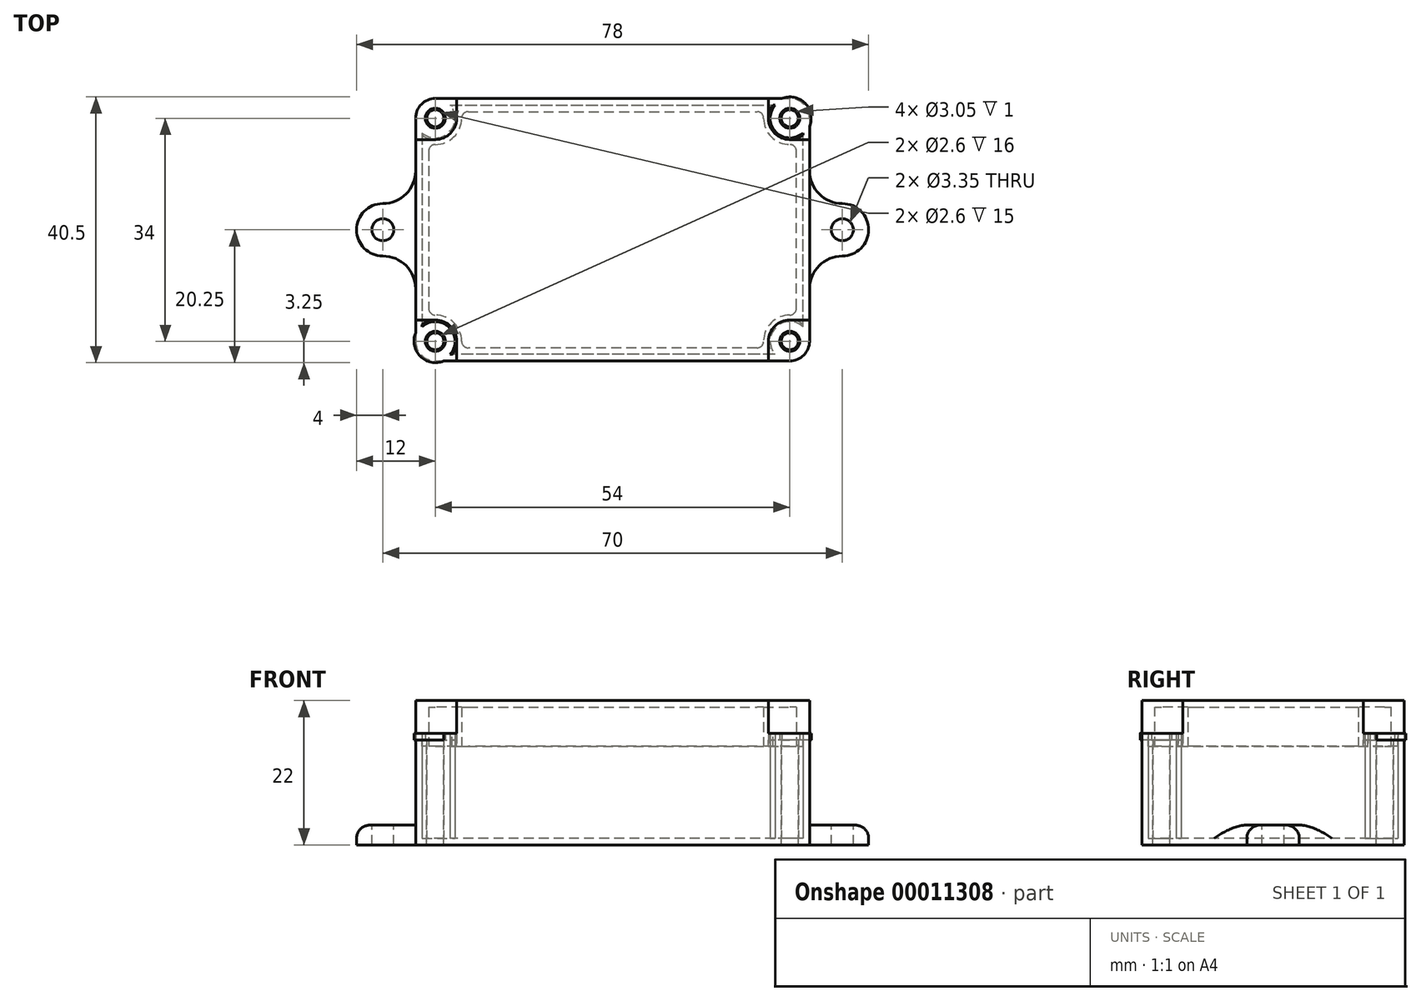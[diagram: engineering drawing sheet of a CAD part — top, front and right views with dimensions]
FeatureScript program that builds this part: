
annotation { "Feature Type Name" : "Feature", "Feature Type Description" : "" }
export const myFeature = defineFeature(function(context is Context, id is Id, definition is map)
    precondition{}
    {
        {
            var Q0;
            Q0=qCreatedBy(makeId("Top.planeOp"),FACE);
            var sketch = newSketch(context, id + "F0", { "sketchPlane" : qUnion([Q0])});
            skLineSegment(sketch, "E0.bottom", {"start": v(-27, 20) * mm, "end": v(27, 20) * mm});
            skLineSegment(sketch, "E0.top", {"start": v(-27, -20) * mm, "end": v(27, -20) * mm});
            skLineSegment(sketch, "E0.left", {"start": v(-30, 17) * mm, "end": v(-30, -17) * mm});
            skLineSegment(sketch, "E0.right", {"start": v(30, 17) * mm, "end": v(30, -17) * mm});
            skLineSegment(sketch, "E1", {"start": v(0, 0) * mm, "end": v(0, 30.82) * mm, "construction": true});
            skLineSegment(sketch, "E2", {"start": v(0, 0) * mm, "end": v(-60.1, 0) * mm, "construction": true});
            skArc(sketch, "E3", {"start": v(-27, 20) * mm, "mid": v(-29.12, 19.12) * mm, "end": v(-30, 17) * mm});
            skLineSegment(sketch, "E4", {"start": v(-30, -4) * mm, "end": v(-35, -4) * mm});
            skLineSegment(sketch, "E5", {"start": v(-30, 4) * mm, "end": v(-35, 4) * mm});
            skArc(sketch, "E6", {"start": v(-35, 4) * mm, "mid": v(-39, 0) * mm, "end": v(-35, -4) * mm});
            skCircle(sketch, "E7", {"center": v(-35, 0) * mm, "radius": 1.68 * mm});
            skLineSegment(sketch, "E8.0.MirrorCS", {"start": v(30, 4) * mm, "end": v(35, 4) * mm});
            skArc(sketch, "E9.0.MirrorCS", {"start": v(35, 4) * mm, "mid": v(39, 0) * mm, "end": v(35, -4) * mm});
            skCircle(sketch, "E10.0.MirrorC", {"center": v(35, 0) * mm, "radius": 1.68 * mm});
            skLineSegment(sketch, "E11.0.MirrorCS", {"start": v(30, -4) * mm, "end": v(35, -4) * mm});
            skCircle(sketch, "E12", {"center": v(-27, 17) * mm, "radius": 1.3 * mm});
            skLineSegment(sketch, "E13", {"start": v(-24.76, 19) * mm, "end": v(0, 19) * mm});
            skLineSegment(sketch, "E14", {"start": v(-29, 0) * mm, "end": v(-29, 14.76) * mm});
            skArc(sketch, "E15.trimOffspring", {"start": v(-29, 14.76) * mm, "mid": v(-24.88, 14.88) * mm, "end": v(-24.76, 19) * mm});
            skLineSegment(sketch, "E16.0.MirrorCS", {"start": v(24.76, 19) * mm, "end": v(0, 19) * mm});
            skArc(sketch, "E17.0.MirrorCS", {"start": v(29, 14.76) * mm, "mid": v(24.88, 14.88) * mm, "end": v(24.76, 19) * mm});
            skLineSegment(sketch, "E18.0.MirrorCS", {"start": v(29, 0) * mm, "end": v(29, 14.76) * mm});
            skCircle(sketch, "E19.0.MirrorC", {"center": v(27, 17) * mm, "radius": 1.3 * mm});
            skArc(sketch, "E20.0.MirrorCS", {"start": v(27, 20) * mm, "mid": v(29.12, 19.12) * mm, "end": v(30, 17) * mm});
            skLineSegment(sketch, "E21.0.MirrorCS", {"start": v(-29, 0) * mm, "end": v(-29, -14.76) * mm});
            skArc(sketch, "E22.0.MirrorCS", {"start": v(-29, -14.76) * mm, "mid": v(-24.88, -14.88) * mm, "end": v(-24.76, -19) * mm});
            skCircle(sketch, "E23.0.MirrorC", {"center": v(-27, -17) * mm, "radius": 1.3 * mm});
            skArc(sketch, "E24.0.MirrorCS", {"start": v(-27, -20) * mm, "mid": v(-29.12, -19.12) * mm, "end": v(-30, -17) * mm});
            skLineSegment(sketch, "E25.0.MirrorCS", {"start": v(-24.76, -19) * mm, "end": v(0, -19) * mm});
            skArc(sketch, "E26.0.MirrorCS", {"start": v(29, -14.76) * mm, "mid": v(24.88, -14.88) * mm, "end": v(24.76, -19) * mm});
            skCircle(sketch, "E27.0.MirrorC", {"center": v(27, -17) * mm, "radius": 1.3 * mm});
            skLineSegment(sketch, "E28.0.MirrorCS", {"start": v(24.76, -19) * mm, "end": v(0, -19) * mm});
            skLineSegment(sketch, "E29.0.MirrorCS", {"start": v(29, 0) * mm, "end": v(29, -14.76) * mm});
            skArc(sketch, "E30.0.MirrorCS", {"start": v(27, -20) * mm, "mid": v(29.12, -19.12) * mm, "end": v(30, -17) * mm});
            skSolve(sketch);
        }
        {
            var Q0;
            {var subQ1=sQuery(id+"F0.wireOp",EDGE,"E4");Q0=makeQuery(id+"F0.imprint","IMPRINT",FACE,{"disambiguationData":[TD([[makeQuery(id+"F0.imprint","IMPRINT",EDGE,{"derivedFrom":subQ1}),-1.0]])]});}
            var Q1;
            Q1=makeQuery(id+"F0.imprint","IMPRINT",FACE,{"disambiguationData":[TD([[makeQuery(id+"F0.imprint","IMPRINT",EDGE,{"derivedFrom":sQuery(id+"F0.wireOp",EDGE,"E0.bottom")}),-1.0]])]});
            var Q2;
            Q2=makeQuery(id+"F0.imprint","IMPRINT",FACE,{"disambiguationData":[TD([[makeQuery(id+"F0.imprint","IMPRINT",EDGE,{"derivedFrom":sQuery(id+"F0.wireOp",EDGE,"E12")}),1.0]])]});
            var Q3;
            Q3=makeQuery(id+"F0.imprint","IMPRINT",FACE,{"disambiguationData":[TD([[makeQuery(id+"F0.imprint","IMPRINT",EDGE,{"derivedFrom":sQuery(id+"F0.wireOp",EDGE,"E23.0.MirrorC")}),-1.0]])]});
            var Q4;
            Q4=makeQuery(id+"F0.imprint","IMPRINT",FACE,{"disambiguationData":[TD([[makeQuery(id+"F0.imprint","IMPRINT",EDGE,{"derivedFrom":sQuery(id+"F0.wireOp",EDGE,"E13")}),-1.0]])]});
            var Q5;
            Q5=makeQuery(id+"F0.imprint","IMPRINT",FACE,{"disambiguationData":[TD([[makeQuery(id+"F0.imprint","IMPRINT",EDGE,{"derivedFrom":sQuery(id+"F0.wireOp",EDGE,"E19.0.MirrorC")}),-1.0]])]});
            var Q6;
            Q6=makeQuery(id+"F0.imprint","IMPRINT",FACE,{"disambiguationData":[TD([[makeQuery(id+"F0.imprint","IMPRINT",EDGE,{"derivedFrom":sQuery(id+"F0.wireOp",EDGE,"E27.0.MirrorC")}),1.0]])]});
            var Q7;
            {var subQ1=sQuery(id+"F0.wireOp",EDGE,"E8.0.MirrorCS");Q7=makeQuery(id+"F0.imprint","IMPRINT",FACE,{"disambiguationData":[TD([[makeQuery(id+"F0.imprint","IMPRINT",EDGE,{"derivedFrom":subQ1}),-1.0]])]});}
            extrude(context, id + "F1", {"entities" : qUnion([Q0, Q1, Q2, Q3, Q4, Q5, Q6, Q7]), "oppositeDirection" : true, "depth" : 1 * mm});
        }
        {
            var Q0;
            Q0=makeQuery(id+"F1.opExtrude","SWEPT_EDGE",EDGE,{"disambiguationData":[OSD([sQuery(id+"F0.wireOp",EDGE,"E0.left"),sQuery(id+"F0.wireOp",EDGE,"E5")])]});
            var Q1;
            Q1=makeQuery(id+"F1.opExtrude","SWEPT_EDGE",EDGE,{"disambiguationData":[OSD([sQuery(id+"F0.wireOp",EDGE,"E0.left"),sQuery(id+"F0.wireOp",EDGE,"E4")])]});
            var Q2;
            Q2=makeQuery(id+"F1.opExtrude","SWEPT_EDGE",EDGE,{"disambiguationData":[OSD([sQuery(id+"F0.wireOp",EDGE,"E0.right"),sQuery(id+"F0.wireOp",EDGE,"E11.0.MirrorCS")])]});
            var Q3;
            Q3=makeQuery(id+"F1.opExtrude","SWEPT_EDGE",EDGE,{"disambiguationData":[OSD([sQuery(id+"F0.wireOp",EDGE,"E0.right"),sQuery(id+"F0.wireOp",EDGE,"E8.0.MirrorCS")])]});
            fillet(context, id + "F2", {"entities" : qUnion([Q0, Q1, Q2, Q3]), "radius" : 5 * mm, "tangentPropagation" : true, "allowEdgeOverflow" : false});
        }
        {
            var Q0;
            Q0=makeQuery(id+"F0.imprint","IMPRINT",FACE,{"disambiguationData":[TD([[makeQuery(id+"F0.imprint","IMPRINT",EDGE,{"derivedFrom":sQuery(id+"F0.wireOp",EDGE,"E0.bottom")}),-1.0]])]});
            extrude(context, id + "F3", {"entities" : qUnion([Q0]), "operationType" : NewBodyOperationType.ADD, "depth" : 15 * mm});
        }
        {
            var Q0;
            {var subQ0=sQuery(id+"F0.wireOp",EDGE,"E0.left");var subQ1=sQuery(id+"F0.wireOp",EDGE,"E3");var subQ2=sQuery(id+"F0.wireOp",EDGE,"E4");var subQ3=sQuery(id+"F0.wireOp",EDGE,"E5");var subQ4=sQuery(id+"F0.wireOp",EDGE,"E6");var subQ5=sQuery(id+"F0.wireOp",EDGE,"E7");var subQ6=sQuery(id+"F0.wireOp",EDGE,"E24.0.MirrorCS");Q0=makeQuery(id+"F3.boolean.opBoolean","SPLIT",FACE,{"disambiguationData":[TD([makeQuery(id+"F1.opExtrude","SWEPT_FACE",FACE,{"disambiguationData":[OSD([subQ4])]})])],"derivedFrom":makeQuery(id+"F1.opExtrude","CAP_FACE",FACE,{"disambiguationData":[OSD([sQuery(id+"F0.wireOp",EDGE,"E0.bottom"),sQuery(id+"F0.wireOp",EDGE,"E0.top"),subQ0,sQuery(id+"F0.wireOp",EDGE,"E0.right"),subQ1,subQ2,subQ3,subQ4,subQ5,sQuery(id+"F0.wireOp",EDGE,"E8.0.MirrorCS"),sQuery(id+"F0.wireOp",EDGE,"E9.0.MirrorCS"),sQuery(id+"F0.wireOp",EDGE,"E10.0.MirrorC"),sQuery(id+"F0.wireOp",EDGE,"E11.0.MirrorCS"),sQuery(id+"F0.wireOp",EDGE,"E20.0.MirrorCS"),subQ6,sQuery(id+"F0.wireOp",EDGE,"E30.0.MirrorCS")])],"isStart":true})});}
            var Q1;
            {var subQ0=sQuery(id+"F0.wireOp",EDGE,"E0.right");var subQ1=sQuery(id+"F0.wireOp",EDGE,"E8.0.MirrorCS");var subQ2=sQuery(id+"F0.wireOp",EDGE,"E9.0.MirrorCS");var subQ3=sQuery(id+"F0.wireOp",EDGE,"E10.0.MirrorC");var subQ4=sQuery(id+"F0.wireOp",EDGE,"E11.0.MirrorCS");var subQ5=sQuery(id+"F0.wireOp",EDGE,"E20.0.MirrorCS");var subQ6=sQuery(id+"F0.wireOp",EDGE,"E30.0.MirrorCS");Q1=makeQuery(id+"F3.boolean.opBoolean","SPLIT",FACE,{"disambiguationData":[TD([makeQuery(id+"F1.opExtrude","SWEPT_FACE",FACE,{"disambiguationData":[OSD([subQ2])]})])],"derivedFrom":makeQuery(id+"F1.opExtrude","CAP_FACE",FACE,{"disambiguationData":[OSD([sQuery(id+"F0.wireOp",EDGE,"E0.bottom"),sQuery(id+"F0.wireOp",EDGE,"E0.top"),sQuery(id+"F0.wireOp",EDGE,"E0.left"),subQ0,sQuery(id+"F0.wireOp",EDGE,"E3"),sQuery(id+"F0.wireOp",EDGE,"E4"),sQuery(id+"F0.wireOp",EDGE,"E5"),sQuery(id+"F0.wireOp",EDGE,"E6"),sQuery(id+"F0.wireOp",EDGE,"E7"),subQ1,subQ2,subQ3,subQ4,subQ5,sQuery(id+"F0.wireOp",EDGE,"E24.0.MirrorCS"),subQ6])],"isStart":true})});}
            extrude(context, id + "F4", {"entities" : qUnion([Q0, Q1]), "operationType" : NewBodyOperationType.ADD, "depth" : 2 * mm});
        }
        {
            var Q0;
            Q0=makeQuery(id+"F4.opExtrude","CAP_EDGE",EDGE,{"disambiguationData":[OSD([sQuery(id+"F0.wireOp",EDGE,"E0.left")])],"isStart":false});
            var Q1;
            Q1=makeQuery(id+"F4.opExtrude","CAP_EDGE",EDGE,{"disambiguationData":[OSD([sQuery(id+"F0.wireOp",EDGE,"E0.right")])],"isStart":false});
            fillet(context, id + "F5", {"entities" : qUnion([Q0, Q1]), "radius" : 2 * mm, "tangentPropagation" : true, "allowEdgeOverflow" : false});
        }
        {
            var Q0;
            Q0=makeQuery(id+"F3.opExtrude","CAP_FACE",FACE,{"disambiguationData":[OSD([sQuery(id+"F0.wireOp",EDGE,"E0.bottom"),sQuery(id+"F0.wireOp",EDGE,"E0.top"),sQuery(id+"F0.wireOp",EDGE,"E0.left"),sQuery(id+"F0.wireOp",EDGE,"E0.right"),sQuery(id+"F0.wireOp",EDGE,"E3"),sQuery(id+"F0.wireOp",EDGE,"E12"),sQuery(id+"F0.wireOp",EDGE,"E13"),sQuery(id+"F0.wireOp",EDGE,"E14"),sQuery(id+"F0.wireOp",EDGE,"E15.trimOffspring"),sQuery(id+"F0.wireOp",EDGE,"E16.0.MirrorCS"),sQuery(id+"F0.wireOp",EDGE,"E17.0.MirrorCS"),sQuery(id+"F0.wireOp",EDGE,"E18.0.MirrorCS"),sQuery(id+"F0.wireOp",EDGE,"E19.0.MirrorC"),sQuery(id+"F0.wireOp",EDGE,"E20.0.MirrorCS"),sQuery(id+"F0.wireOp",EDGE,"E21.0.MirrorCS"),sQuery(id+"F0.wireOp",EDGE,"E22.0.MirrorCS"),sQuery(id+"F0.wireOp",EDGE,"E23.0.MirrorC"),sQuery(id+"F0.wireOp",EDGE,"E24.0.MirrorCS"),sQuery(id+"F0.wireOp",EDGE,"E25.0.MirrorCS"),sQuery(id+"F0.wireOp",EDGE,"E26.0.MirrorCS"),sQuery(id+"F0.wireOp",EDGE,"E27.0.MirrorC"),sQuery(id+"F0.wireOp",EDGE,"E28.0.MirrorCS"),sQuery(id+"F0.wireOp",EDGE,"E29.0.MirrorCS"),sQuery(id+"F0.wireOp",EDGE,"E30.0.MirrorCS")])],"isStart":false});
            var sketch = newSketch(context, id + "F6", { "sketchPlane" : qUnion([Q0])});
            skLineSegment(sketch, "E31.1", {"start": v(-27, 20) * mm, "end": v(27, 20) * mm});
            skArc(sketch, "E31.2", {"start": v(-27, 20) * mm, "mid": v(-29.12, 19.12) * mm, "end": v(-30, 17) * mm});
            skLineSegment(sketch, "E31.3", {"start": v(-30, 17) * mm, "end": v(-30, -17) * mm});
            skArc(sketch, "E31.4", {"start": v(-27, -20) * mm, "mid": v(-29.12, -19.12) * mm, "end": v(-30, -17) * mm});
            skLineSegment(sketch, "E31.5", {"start": v(-27, -20) * mm, "end": v(27, -20) * mm});
            skArc(sketch, "E31.6", {"start": v(27, -20) * mm, "mid": v(29.12, -19.12) * mm, "end": v(30, -17) * mm});
            skLineSegment(sketch, "E31.7", {"start": v(30, 17) * mm, "end": v(30, -17) * mm});
            skArc(sketch, "E31.8", {"start": v(27, 20) * mm, "mid": v(29.12, 19.12) * mm, "end": v(30, 17) * mm});
            skCircle(sketch, "E31.9", {"center": v(27, 17) * mm, "radius": 1.3 * mm});
            skArc(sketch, "E31.10", {"start": v(29, 14.76) * mm, "mid": v(24.88, 14.88) * mm, "end": v(24.76, 19) * mm});
            skLineSegment(sketch, "E31.11", {"start": v(29, -14.76) * mm, "end": v(29, 14.76) * mm});
            skArc(sketch, "E31.12", {"start": v(29, -14.76) * mm, "mid": v(24.88, -14.88) * mm, "end": v(24.76, -19) * mm});
            skLineSegment(sketch, "E31.13", {"start": v(24.76, -19) * mm, "end": v(-24.76, -19) * mm});
            skCircle(sketch, "E31.14", {"center": v(27, -17) * mm, "radius": 1.3 * mm});
            skArc(sketch, "E31.15", {"start": v(-29, -14.76) * mm, "mid": v(-24.88, -14.88) * mm, "end": v(-24.76, -19) * mm});
            skCircle(sketch, "E31.16", {"center": v(-27, -17) * mm, "radius": 1.3 * mm});
            skLineSegment(sketch, "E31.17", {"start": v(-29, 14.76) * mm, "end": v(-29, -14.76) * mm});
            skArc(sketch, "E31.18", {"start": v(-29, 14.76) * mm, "mid": v(-24.88, 14.88) * mm, "end": v(-24.76, 19) * mm});
            skCircle(sketch, "E31.20", {"center": v(-27, 17) * mm, "radius": 1.3 * mm});
            skLineSegment(sketch, "E31.21", {"start": v(-24.76, 19) * mm, "end": v(24.76, 19) * mm});
            skLineSegment(sketch, "E32.0", {"start": v(0, 0) * mm, "end": v(0, 30.82) * mm, "construction": true});
            skLineSegment(sketch, "E32.1", {"start": v(0, 0) * mm, "end": v(-60.1, 0) * mm, "construction": true});
            skCircle(sketch, "E33", {"center": v(-27, 17) * mm, "radius": 3.25 * mm});
            skCircle(sketch, "E34", {"center": v(-27, 17) * mm, "radius": 1.52 * mm});
            skCircle(sketch, "E35.0.MirrorC", {"center": v(27, 17) * mm, "radius": 1.52 * mm});
            skCircle(sketch, "E36.0.MirrorC", {"center": v(27, 17) * mm, "radius": 3.25 * mm});
            skCircle(sketch, "E37.0.MirrorC", {"center": v(-27, -17) * mm, "radius": 1.52 * mm});
            skCircle(sketch, "E38.0.MirrorC", {"center": v(-27, -17) * mm, "radius": 3.25 * mm});
            skCircle(sketch, "E39.0.MirrorC", {"center": v(27, -17) * mm, "radius": 1.52 * mm});
            skCircle(sketch, "E40.0.MirrorC", {"center": v(27, -17) * mm, "radius": 3.25 * mm});
            skArc(sketch, "E41.0", {"start": v(-28, 13.13) * mm, "mid": v(-24.17, 14.17) * mm, "end": v(-23.13, 18) * mm});
            skLineSegment(sketch, "E41.1", {"start": v(-28, 13.13) * mm, "end": v(-28, -13.13) * mm});
            skArc(sketch, "E41.2", {"start": v(-28, -13.13) * mm, "mid": v(-24.17, -14.17) * mm, "end": v(-23.13, -18) * mm});
            skLineSegment(sketch, "E41.3", {"start": v(23.13, -18) * mm, "end": v(-23.13, -18) * mm});
            skArc(sketch, "E41.4", {"start": v(28, -13.13) * mm, "mid": v(24.17, -14.17) * mm, "end": v(23.13, -18) * mm});
            skLineSegment(sketch, "E41.5", {"start": v(-23.13, 18) * mm, "end": v(23.13, 18) * mm});
            skLineSegment(sketch, "E41.6", {"start": v(28, -13.13) * mm, "end": v(28, 13.13) * mm});
            skArc(sketch, "E41.7", {"start": v(28, 13.13) * mm, "mid": v(24.17, 14.17) * mm, "end": v(23.13, 18) * mm});
            skLineSegment(sketch, "E42", {"start": v(-30, 13.75) * mm, "end": v(-27, 13.75) * mm});
            skLineSegment(sketch, "E43", {"start": v(-23.75, 20) * mm, "end": v(-23.75, 17) * mm});
            skLineSegment(sketch, "E44.0.MirrorCS", {"start": v(23.75, 20) * mm, "end": v(23.75, 17) * mm});
            skLineSegment(sketch, "E45.0.MirrorCS", {"start": v(30, 13.75) * mm, "end": v(27, 13.75) * mm});
            skLineSegment(sketch, "E46.0.MirrorCS", {"start": v(-30, -13.75) * mm, "end": v(-27, -13.75) * mm});
            skLineSegment(sketch, "E47.0.MirrorCS", {"start": v(-23.75, -20) * mm, "end": v(-23.75, -17) * mm});
            skLineSegment(sketch, "E48.0.MirrorCS", {"start": v(23.75, -20) * mm, "end": v(23.75, -17) * mm});
            skLineSegment(sketch, "E49.0.MirrorCS", {"start": v(30, -13.75) * mm, "end": v(27, -13.75) * mm});
            skSolve(sketch);
        }
        {
            var Q0;
            {var subQ3=sQuery(id+"F6.wireOp",EDGE,"E31.1");var subQ5=sQuery(id+"F6.wireOp",EDGE,"E43");var subQ7=makeQuery(id+"F6.imprint","INTERSECT",VERTEX,{"derivedFrom":[subQ3,subQ5]});Q0=makeQuery(id+"F6.imprint","IMPRINT",FACE,{"disambiguationData":[TD([[makeQuery(id+"F6.imprint","IMPRINT",EDGE,{"disambiguationData":[TD([[subQ7,-1.0]])],"derivedFrom":subQ3}),-1.0]])]});}
            var Q1;
            {var subQ0=sQuery(id+"F6.wireOp",EDGE,"E44.0.MirrorCS");var subQ3=sQuery(id+"F6.wireOp",EDGE,"E31.1");var subQ4=makeQuery(id+"F6.imprint","INTERSECT",VERTEX,{"derivedFrom":[subQ3,subQ0]});Q1=makeQuery(id+"F6.imprint","IMPRINT",FACE,{"disambiguationData":[TD([[makeQuery(id+"F6.imprint","IMPRINT",EDGE,{"disambiguationData":[TD([[subQ4,-1.0]])],"derivedFrom":subQ3}),-1.0]])]});}
            var Q2;
            {var subQ10=sQuery(id+"F6.wireOp",EDGE,"E31.8");Q2=makeQuery(id+"F6.imprint","IMPRINT",FACE,{"disambiguationData":[TD([[makeQuery(id+"F6.imprint","IMPRINT",EDGE,{"derivedFrom":subQ10}),-1.0]])]});}
            var Q3;
            {var subQ10=sQuery(id+"F6.wireOp",EDGE,"E31.6");Q3=makeQuery(id+"F6.imprint","IMPRINT",FACE,{"disambiguationData":[TD([[makeQuery(id+"F6.imprint","IMPRINT",EDGE,{"derivedFrom":subQ10}),1.0]])]});}
            var Q4;
            {var subQ8=sQuery(id+"F6.wireOp",EDGE,"E31.4");Q4=makeQuery(id+"F6.imprint","IMPRINT",FACE,{"disambiguationData":[TD([[makeQuery(id+"F6.imprint","IMPRINT",EDGE,{"derivedFrom":subQ8}),-1.0]])]});}
            var Q5;
            {var subQ7=sQuery(id+"F6.wireOp",EDGE,"E31.10");Q5=makeQuery(id+"F6.imprint","IMPRINT",FACE,{"disambiguationData":[TD([[makeQuery(id+"F6.imprint","IMPRINT",EDGE,{"derivedFrom":subQ7}),1.0]])]});}
            var Q6;
            Q6=makeQuery(id+"F6.imprint","IMPRINT",FACE,{"disambiguationData":[TD([[makeQuery(id+"F6.imprint","IMPRINT",EDGE,{"derivedFrom":sQuery(id+"F6.wireOp",EDGE,"E41.0")}),1.0]])]});
            var Q7;
            {var subQ1=sQuery(id+"F6.wireOp",EDGE,"E31.21");var subQ3=sQuery(id+"F6.wireOp",EDGE,"E33");var subQ5=makeQuery(id+"F6.imprint","INTERSECT",VERTEX,{"derivedFrom":[subQ1,subQ3]});Q7=makeQuery(id+"F6.imprint","IMPRINT",FACE,{"disambiguationData":[TD([[makeQuery(id+"F6.imprint","IMPRINT",EDGE,{"disambiguationData":[TD([[subQ5,-1.0]])],"derivedFrom":subQ1}),-1.0]])]});}
            var Q8;
            {var subQ0=sQuery(id+"F6.wireOp",EDGE,"E43");var subQ3=sQuery(id+"F6.wireOp",EDGE,"E31.1");var subQ4=makeQuery(id+"F6.imprint","INTERSECT",VERTEX,{"derivedFrom":[subQ3,subQ0]});Q8=makeQuery(id+"F6.imprint","IMPRINT",FACE,{"disambiguationData":[TD([[makeQuery(id+"F6.imprint","IMPRINT",EDGE,{"disambiguationData":[TD([[subQ4,1.0]])],"derivedFrom":subQ3}),-1.0]])]});}
            var Q9;
            {var subQ0=sQuery(id+"F6.wireOp",EDGE,"E42");var subQ3=sQuery(id+"F6.wireOp",EDGE,"E31.3");var subQ4=makeQuery(id+"F6.imprint","INTERSECT",VERTEX,{"derivedFrom":[subQ3,subQ0]});Q9=makeQuery(id+"F6.imprint","IMPRINT",FACE,{"disambiguationData":[TD([[makeQuery(id+"F6.imprint","IMPRINT",EDGE,{"disambiguationData":[TD([[subQ4,1.0]])],"derivedFrom":subQ3}),1.0]])]});}
            var Q10;
            {var subQ0=sQuery(id+"F6.wireOp",EDGE,"E33");var subQ1=sQuery(id+"F6.wireOp",EDGE,"E31.17");var subQ2=makeQuery(id+"F6.imprint","INTERSECT",VERTEX,{"derivedFrom":[subQ1,subQ0]});Q10=makeQuery(id+"F6.imprint","IMPRINT",FACE,{"disambiguationData":[TD([[makeQuery(id+"F6.imprint","IMPRINT",EDGE,{"disambiguationData":[TD([[subQ2,-1.0]])],"derivedFrom":subQ1}),1.0]])]});}
            var Q11;
            {var subQ10=sQuery(id+"F6.wireOp",EDGE,"E31.2");Q11=makeQuery(id+"F6.imprint","IMPRINT",FACE,{"disambiguationData":[TD([[makeQuery(id+"F6.imprint","IMPRINT",EDGE,{"derivedFrom":subQ10}),1.0]])]});}
            var Q12;
            {var subQ7=sQuery(id+"F6.wireOp",EDGE,"E31.18");Q12=makeQuery(id+"F6.imprint","IMPRINT",FACE,{"disambiguationData":[TD([[makeQuery(id+"F6.imprint","IMPRINT",EDGE,{"derivedFrom":subQ7}),-1.0]])]});}
            var Q13;
            {var subQ3=sQuery(id+"F6.wireOp",EDGE,"E31.3");var subQ5=sQuery(id+"F6.wireOp",EDGE,"E42");var subQ7=makeQuery(id+"F6.imprint","INTERSECT",VERTEX,{"derivedFrom":[subQ3,subQ5]});Q13=makeQuery(id+"F6.imprint","IMPRINT",FACE,{"disambiguationData":[TD([[makeQuery(id+"F6.imprint","IMPRINT",EDGE,{"disambiguationData":[TD([[subQ7,-1.0]])],"derivedFrom":subQ3}),1.0]])]});}
            var Q14;
            {var subQ0=sQuery(id+"F6.wireOp",EDGE,"E46.0.MirrorCS");var subQ3=sQuery(id+"F6.wireOp",EDGE,"E31.3");var subQ4=makeQuery(id+"F6.imprint","INTERSECT",VERTEX,{"derivedFrom":[subQ3,subQ0]});Q14=makeQuery(id+"F6.imprint","IMPRINT",FACE,{"disambiguationData":[TD([[makeQuery(id+"F6.imprint","IMPRINT",EDGE,{"disambiguationData":[TD([[subQ4,-1.0]])],"derivedFrom":subQ3}),1.0]])]});}
            var Q15;
            {var subQ0=sQuery(id+"F6.wireOp",EDGE,"E46.0.MirrorCS");var subQ1=sQuery(id+"F6.wireOp",EDGE,"E31.17");var subQ2=makeQuery(id+"F6.imprint","INTERSECT",VERTEX,{"derivedFrom":[subQ1,subQ0]});Q15=makeQuery(id+"F6.imprint","IMPRINT",FACE,{"disambiguationData":[TD([[makeQuery(id+"F6.imprint","IMPRINT",EDGE,{"disambiguationData":[TD([[subQ2,-1.0]])],"derivedFrom":subQ1}),1.0]])]});}
            var Q16;
            {var subQ7=sQuery(id+"F6.wireOp",EDGE,"E31.15");Q16=makeQuery(id+"F6.imprint","IMPRINT",FACE,{"disambiguationData":[TD([[makeQuery(id+"F6.imprint","IMPRINT",EDGE,{"derivedFrom":subQ7}),1.0]])]});}
            var Q17;
            {var subQ0=sQuery(id+"F6.wireOp",EDGE,"E47.0.MirrorCS");var subQ1=sQuery(id+"F6.wireOp",EDGE,"E31.13");var subQ2=makeQuery(id+"F6.imprint","INTERSECT",VERTEX,{"derivedFrom":[subQ1,subQ0]});Q17=makeQuery(id+"F6.imprint","IMPRINT",FACE,{"disambiguationData":[TD([[makeQuery(id+"F6.imprint","IMPRINT",EDGE,{"disambiguationData":[TD([[subQ2,-1.0]])],"derivedFrom":subQ1}),-1.0]])]});}
            var Q18;
            {var subQ0=sQuery(id+"F6.wireOp",EDGE,"E47.0.MirrorCS");var subQ3=sQuery(id+"F6.wireOp",EDGE,"E31.5");var subQ4=makeQuery(id+"F6.imprint","INTERSECT",VERTEX,{"derivedFrom":[subQ3,subQ0]});Q18=makeQuery(id+"F6.imprint","IMPRINT",FACE,{"disambiguationData":[TD([[makeQuery(id+"F6.imprint","IMPRINT",EDGE,{"disambiguationData":[TD([[subQ4,1.0]])],"derivedFrom":subQ3}),1.0]])]});}
            var Q19;
            {var subQ3=sQuery(id+"F6.wireOp",EDGE,"E31.5");var subQ5=sQuery(id+"F6.wireOp",EDGE,"E47.0.MirrorCS");var subQ7=makeQuery(id+"F6.imprint","INTERSECT",VERTEX,{"derivedFrom":[subQ3,subQ5]});Q19=makeQuery(id+"F6.imprint","IMPRINT",FACE,{"disambiguationData":[TD([[makeQuery(id+"F6.imprint","IMPRINT",EDGE,{"disambiguationData":[TD([[subQ7,-1.0]])],"derivedFrom":subQ3}),1.0]])]});}
            var Q20;
            {var subQ0=sQuery(id+"F6.wireOp",EDGE,"E48.0.MirrorCS");var subQ3=sQuery(id+"F6.wireOp",EDGE,"E31.5");var subQ4=makeQuery(id+"F6.imprint","INTERSECT",VERTEX,{"derivedFrom":[subQ3,subQ0]});Q20=makeQuery(id+"F6.imprint","IMPRINT",FACE,{"disambiguationData":[TD([[makeQuery(id+"F6.imprint","IMPRINT",EDGE,{"disambiguationData":[TD([[subQ4,-1.0]])],"derivedFrom":subQ3}),1.0]])]});}
            var Q21;
            {var subQ1=sQuery(id+"F6.wireOp",EDGE,"E31.13");var subQ3=sQuery(id+"F6.wireOp",EDGE,"E40.0.MirrorC");var subQ5=makeQuery(id+"F6.imprint","INTERSECT",VERTEX,{"derivedFrom":[subQ1,subQ3]});Q21=makeQuery(id+"F6.imprint","IMPRINT",FACE,{"disambiguationData":[TD([[makeQuery(id+"F6.imprint","IMPRINT",EDGE,{"disambiguationData":[TD([[subQ5,-1.0]])],"derivedFrom":subQ1}),-1.0]])]});}
            var Q22;
            {var subQ7=sQuery(id+"F6.wireOp",EDGE,"E31.12");Q22=makeQuery(id+"F6.imprint","IMPRINT",FACE,{"disambiguationData":[TD([[makeQuery(id+"F6.imprint","IMPRINT",EDGE,{"derivedFrom":subQ7}),-1.0]])]});}
            var Q23;
            {var subQ1=sQuery(id+"F6.wireOp",EDGE,"E31.11");var subQ3=sQuery(id+"F6.wireOp",EDGE,"E40.0.MirrorC");var subQ5=makeQuery(id+"F6.imprint","INTERSECT",VERTEX,{"derivedFrom":[subQ1,subQ3]});Q23=makeQuery(id+"F6.imprint","IMPRINT",FACE,{"disambiguationData":[TD([[makeQuery(id+"F6.imprint","IMPRINT",EDGE,{"disambiguationData":[TD([[subQ5,-1.0]])],"derivedFrom":subQ1}),1.0]])]});}
            var Q24;
            {var subQ0=sQuery(id+"F6.wireOp",EDGE,"E49.0.MirrorCS");var subQ3=sQuery(id+"F6.wireOp",EDGE,"E31.7");var subQ4=makeQuery(id+"F6.imprint","INTERSECT",VERTEX,{"derivedFrom":[subQ3,subQ0]});Q24=makeQuery(id+"F6.imprint","IMPRINT",FACE,{"disambiguationData":[TD([[makeQuery(id+"F6.imprint","IMPRINT",EDGE,{"disambiguationData":[TD([[subQ4,-1.0]])],"derivedFrom":subQ3}),-1.0]])]});}
            var Q25;
            {var subQ3=sQuery(id+"F6.wireOp",EDGE,"E31.7");var subQ5=sQuery(id+"F6.wireOp",EDGE,"E45.0.MirrorCS");var subQ7=makeQuery(id+"F6.imprint","INTERSECT",VERTEX,{"derivedFrom":[subQ3,subQ5]});Q25=makeQuery(id+"F6.imprint","IMPRINT",FACE,{"disambiguationData":[TD([[makeQuery(id+"F6.imprint","IMPRINT",EDGE,{"disambiguationData":[TD([[subQ7,-1.0]])],"derivedFrom":subQ3}),-1.0]])]});}
            var Q26;
            {var subQ0=sQuery(id+"F6.wireOp",EDGE,"E45.0.MirrorCS");var subQ1=sQuery(id+"F6.wireOp",EDGE,"E31.11");var subQ2=makeQuery(id+"F6.imprint","INTERSECT",VERTEX,{"derivedFrom":[subQ1,subQ0]});Q26=makeQuery(id+"F6.imprint","IMPRINT",FACE,{"disambiguationData":[TD([[makeQuery(id+"F6.imprint","IMPRINT",EDGE,{"disambiguationData":[TD([[subQ2,-1.0]])],"derivedFrom":subQ1}),1.0]])]});}
            var Q27;
            {var subQ0=sQuery(id+"F6.wireOp",EDGE,"E45.0.MirrorCS");var subQ3=sQuery(id+"F6.wireOp",EDGE,"E31.7");var subQ4=makeQuery(id+"F6.imprint","INTERSECT",VERTEX,{"derivedFrom":[subQ3,subQ0]});Q27=makeQuery(id+"F6.imprint","IMPRINT",FACE,{"disambiguationData":[TD([[makeQuery(id+"F6.imprint","IMPRINT",EDGE,{"disambiguationData":[TD([[subQ4,1.0]])],"derivedFrom":subQ3}),-1.0]])]});}
            var Q28;
            {var subQ0=sQuery(id+"F6.wireOp",EDGE,"E44.0.MirrorCS");var subQ1=sQuery(id+"F6.wireOp",EDGE,"E31.21");var subQ2=makeQuery(id+"F6.imprint","INTERSECT",VERTEX,{"derivedFrom":[subQ1,subQ0]});Q28=makeQuery(id+"F6.imprint","IMPRINT",FACE,{"disambiguationData":[TD([[makeQuery(id+"F6.imprint","IMPRINT",EDGE,{"disambiguationData":[TD([[subQ2,-1.0]])],"derivedFrom":subQ1}),-1.0]])]});}
            extrude(context, id + "F7", {"entities" : qUnion([Q0, Q1, Q2, Q3, Q4, Q5, Q6, Q7, Q8, Q9, Q10, Q11, Q12, Q13, Q14, Q15, Q16, Q17, Q18, Q19, Q20, Q21, Q22, Q23, Q24, Q25, Q26, Q27, Q28]), "depth" : 1 * mm});
        }
        {
            var Q0;
            Q0=makeQuery(id+"F7.opExtrude","CAP_FACE",FACE,{"disambiguationData":[OSD([sQuery(id+"F6.wireOp",EDGE,"E31.1"),sQuery(id+"F6.wireOp",EDGE,"E31.2"),sQuery(id+"F6.wireOp",EDGE,"E31.3"),sQuery(id+"F6.wireOp",EDGE,"E31.4"),sQuery(id+"F6.wireOp",EDGE,"E31.5"),sQuery(id+"F6.wireOp",EDGE,"E31.6"),sQuery(id+"F6.wireOp",EDGE,"E31.7"),sQuery(id+"F6.wireOp",EDGE,"E31.8"),sQuery(id+"F6.wireOp",EDGE,"E34"),sQuery(id+"F6.wireOp",EDGE,"E35.0.MirrorC"),sQuery(id+"F6.wireOp",EDGE,"E37.0.MirrorC"),sQuery(id+"F6.wireOp",EDGE,"E39.0.MirrorC"),sQuery(id+"F6.wireOp",EDGE,"E41.0"),sQuery(id+"F6.wireOp",EDGE,"E41.1"),sQuery(id+"F6.wireOp",EDGE,"E41.2"),sQuery(id+"F6.wireOp",EDGE,"E41.3"),sQuery(id+"F6.wireOp",EDGE,"E41.4"),sQuery(id+"F6.wireOp",EDGE,"E41.5"),sQuery(id+"F6.wireOp",EDGE,"E41.6"),sQuery(id+"F6.wireOp",EDGE,"E41.7")])],"isStart":false});
            var sketch = newSketch(context, id + "F8", { "sketchPlane" : qUnion([Q0])});
            skLineSegment(sketch, "E50.0", {"start": v(-30, 17) * mm, "end": v(-30, -17) * mm});
            skLineSegment(sketch, "E50.1", {"start": v(-28, 13.13) * mm, "end": v(-28, -13.13) * mm});
            skArc(sketch, "E50.2", {"start": v(-28, 13.13) * mm, "mid": v(-24.17, 14.17) * mm, "end": v(-23.13, 18) * mm});
            skLineSegment(sketch, "E50.3", {"start": v(-23.13, 18) * mm, "end": v(23.13, 18) * mm});
            skLineSegment(sketch, "E50.4", {"start": v(-27, 20) * mm, "end": v(27, 20) * mm});
            skArc(sketch, "E50.5", {"start": v(-27, 20) * mm, "mid": v(-29.12, 19.12) * mm, "end": v(-30, 17) * mm});
            skLineSegment(sketch, "E50.6", {"start": v(-23.75, 20) * mm, "end": v(-23.75, 17) * mm});
            skCircle(sketch, "E50.7", {"center": v(-27, 17) * mm, "radius": 3.25 * mm});
            skLineSegment(sketch, "E50.8", {"start": v(-30, 13.75) * mm, "end": v(-27, 13.75) * mm});
            skLineSegment(sketch, "E50.9", {"start": v(23.75, 20) * mm, "end": v(23.75, 17) * mm});
            skCircle(sketch, "E50.10", {"center": v(27, 17) * mm, "radius": 3.25 * mm});
            skLineSegment(sketch, "E50.11", {"start": v(30, 13.75) * mm, "end": v(27, 13.75) * mm});
            skLineSegment(sketch, "E50.12", {"start": v(30, 17) * mm, "end": v(30, -17) * mm});
            skLineSegment(sketch, "E50.13", {"start": v(28, -13.13) * mm, "end": v(28, 13.13) * mm});
            skArc(sketch, "E50.14", {"start": v(28, 13.13) * mm, "mid": v(24.17, 14.17) * mm, "end": v(23.13, 18) * mm});
            skArc(sketch, "E50.15", {"start": v(28, -13.13) * mm, "mid": v(24.17, -14.17) * mm, "end": v(23.13, -18) * mm});
            skLineSegment(sketch, "E50.16", {"start": v(23.13, -18) * mm, "end": v(-23.13, -18) * mm});
            skArc(sketch, "E50.17", {"start": v(-28, -13.13) * mm, "mid": v(-24.17, -14.17) * mm, "end": v(-23.13, -18) * mm});
            skCircle(sketch, "E50.18", {"center": v(-27, -17) * mm, "radius": 3.25 * mm});
            skLineSegment(sketch, "E50.19", {"start": v(-30, -13.75) * mm, "end": v(-27, -13.75) * mm});
            skLineSegment(sketch, "E50.20", {"start": v(-23.75, -20) * mm, "end": v(-23.75, -17) * mm});
            skLineSegment(sketch, "E50.21", {"start": v(-27, -20) * mm, "end": v(27, -20) * mm});
            skLineSegment(sketch, "E50.22", {"start": v(23.75, -20) * mm, "end": v(23.75, -17) * mm});
            skCircle(sketch, "E50.23", {"center": v(27, -17) * mm, "radius": 3.25 * mm});
            skLineSegment(sketch, "E50.24", {"start": v(30, -13.75) * mm, "end": v(27, -13.75) * mm});
            skArc(sketch, "E50.25", {"start": v(27, -20) * mm, "mid": v(29.12, -19.12) * mm, "end": v(30, -17) * mm});
            skArc(sketch, "E50.26", {"start": v(27, 20) * mm, "mid": v(29.12, 19.12) * mm, "end": v(30, 17) * mm});
            skArc(sketch, "E50.27", {"start": v(-27, -20) * mm, "mid": v(-29.12, -19.12) * mm, "end": v(-30, -17) * mm});
            skSolve(sketch);
        }
        {
            var Q0;
            Q0=makeQuery(id+"F8.imprint","IMPRINT",FACE,{"disambiguationData":[TD([[makeQuery(id+"F8.imprint","IMPRINT",EDGE,{"derivedFrom":sQuery(id+"F8.wireOp",EDGE,"E50.1")}),-1.0]])]});
            extrude(context, id + "F9", {"entities" : qUnion([Q0]), "operationType" : NewBodyOperationType.ADD, "depth" : 4 * mm});
        }
        {
            var Q0;
            Q0=makeQuery(id+"F9.opExtrude","CAP_FACE",FACE,{"disambiguationData":[OSD([sQuery(id+"F8.wireOp",EDGE,"E50.0"),sQuery(id+"F8.wireOp",EDGE,"E50.1"),sQuery(id+"F8.wireOp",EDGE,"E50.2"),sQuery(id+"F8.wireOp",EDGE,"E50.3"),sQuery(id+"F8.wireOp",EDGE,"E50.4"),sQuery(id+"F8.wireOp",EDGE,"E50.6"),sQuery(id+"F8.wireOp",EDGE,"E50.7"),sQuery(id+"F8.wireOp",EDGE,"E50.8"),sQuery(id+"F8.wireOp",EDGE,"E50.9"),sQuery(id+"F8.wireOp",EDGE,"E50.10"),sQuery(id+"F8.wireOp",EDGE,"E50.11"),sQuery(id+"F8.wireOp",EDGE,"E50.12"),sQuery(id+"F8.wireOp",EDGE,"E50.13"),sQuery(id+"F8.wireOp",EDGE,"E50.14"),sQuery(id+"F8.wireOp",EDGE,"E50.15"),sQuery(id+"F8.wireOp",EDGE,"E50.16"),sQuery(id+"F8.wireOp",EDGE,"E50.17"),sQuery(id+"F8.wireOp",EDGE,"E50.18"),sQuery(id+"F8.wireOp",EDGE,"E50.19"),sQuery(id+"F8.wireOp",EDGE,"E50.20"),sQuery(id+"F8.wireOp",EDGE,"E50.21"),sQuery(id+"F8.wireOp",EDGE,"E50.22"),sQuery(id+"F8.wireOp",EDGE,"E50.23"),sQuery(id+"F8.wireOp",EDGE,"E50.24")])],"isStart":false});
            var sketch = newSketch(context, id + "F10", { "sketchPlane" : qUnion([Q0])});
            skLineSegment(sketch, "E51.1", {"start": v(-23.75, 20) * mm, "end": v(23.75, 20) * mm});
            skLineSegment(sketch, "E51.2", {"start": v(-23.75, 20) * mm, "end": v(-23.75, 17) * mm});
            skArc(sketch, "E51.3", {"start": v(-27, 13.75) * mm, "mid": v(-24.7, 14.7) * mm, "end": v(-23.75, 17) * mm});
            skLineSegment(sketch, "E51.4", {"start": v(-30, 13.75) * mm, "end": v(-27, 13.75) * mm});
            skLineSegment(sketch, "E51.5", {"start": v(-30, 13.75) * mm, "end": v(-30, -13.75) * mm});
            skLineSegment(sketch, "E51.6", {"start": v(-30, -13.75) * mm, "end": v(-27, -13.75) * mm});
            skArc(sketch, "E51.7", {"start": v(-27, -13.75) * mm, "mid": v(-24.7, -14.7) * mm, "end": v(-23.75, -17) * mm});
            skLineSegment(sketch, "E51.8", {"start": v(-23.75, -20) * mm, "end": v(-23.75, -17) * mm});
            skLineSegment(sketch, "E51.9", {"start": v(-23.75, -20) * mm, "end": v(23.75, -20) * mm});
            skLineSegment(sketch, "E51.10", {"start": v(23.75, -20) * mm, "end": v(23.75, -17) * mm});
            skArc(sketch, "E51.11", {"start": v(27, -13.75) * mm, "mid": v(24.7, -14.7) * mm, "end": v(23.75, -17) * mm});
            skLineSegment(sketch, "E51.12", {"start": v(30, -13.75) * mm, "end": v(27, -13.75) * mm});
            skLineSegment(sketch, "E51.13", {"start": v(30, 13.75) * mm, "end": v(30, -13.75) * mm});
            skLineSegment(sketch, "E51.14", {"start": v(30, 13.75) * mm, "end": v(27, 13.75) * mm});
            skArc(sketch, "E51.15", {"start": v(27, 13.75) * mm, "mid": v(24.7, 14.7) * mm, "end": v(23.75, 17) * mm});
            skLineSegment(sketch, "E51.16", {"start": v(23.75, 20) * mm, "end": v(23.75, 17) * mm});
            skSolve(sketch);
        }
        {
            var Q0;
            Q0=makeQuery(id+"F10.imprint","IMPRINT",FACE,{"disambiguationData":[TD([[makeQuery(id+"F10.imprint","IMPRINT",EDGE,{"derivedFrom":sQuery(id+"F10.wireOp",EDGE,"E51.1")}),-1.0]])]});
            var Q1;
            Q1=makeQuery(id+"F10.imprint","IMPRINT",FACE,{"disambiguationData":[TD([[makeQuery(id+"F10.imprint","IMPRINT",EDGE,{"derivedFrom":makeQuery(id+"F9.opExtrude","CAP_EDGE",EDGE,{"disambiguationData":[OSD([sQuery(id+"F8.wireOp",EDGE,"E50.1")])],"isStart":false})}),1.0]])]});
            extrude(context, id + "F11", {"entities" : qUnion([Q0, Q1]), "operationType" : NewBodyOperationType.ADD, "depth" : 1 * mm});
        }
        {
            var Q0;
            Q0=makeQuery(id+"F6.imprint","IMPRINT",FACE,{"disambiguationData":[TD([[makeQuery(id+"F6.imprint","IMPRINT",EDGE,{"derivedFrom":sQuery(id+"F6.wireOp",EDGE,"E41.0")}),1.0]])]});
            var Q1;
            {var subQ0=sQuery(id+"F6.wireOp",EDGE,"E44.0.MirrorCS");var subQ1=sQuery(id+"F6.wireOp",EDGE,"E31.21");var subQ2=makeQuery(id+"F6.imprint","INTERSECT",VERTEX,{"derivedFrom":[subQ1,subQ0]});Q1=makeQuery(id+"F6.imprint","IMPRINT",FACE,{"disambiguationData":[TD([[makeQuery(id+"F6.imprint","IMPRINT",EDGE,{"disambiguationData":[TD([[subQ2,-1.0]])],"derivedFrom":subQ1}),-1.0]])]});}
            var Q2;
            {var subQ0=sQuery(id+"F6.wireOp",EDGE,"E45.0.MirrorCS");var subQ1=sQuery(id+"F6.wireOp",EDGE,"E31.11");var subQ2=makeQuery(id+"F6.imprint","INTERSECT",VERTEX,{"derivedFrom":[subQ1,subQ0]});Q2=makeQuery(id+"F6.imprint","IMPRINT",FACE,{"disambiguationData":[TD([[makeQuery(id+"F6.imprint","IMPRINT",EDGE,{"disambiguationData":[TD([[subQ2,-1.0]])],"derivedFrom":subQ1}),1.0]])]});}
            var Q3;
            {var subQ1=sQuery(id+"F6.wireOp",EDGE,"E31.11");var subQ3=sQuery(id+"F6.wireOp",EDGE,"E40.0.MirrorC");var subQ5=makeQuery(id+"F6.imprint","INTERSECT",VERTEX,{"derivedFrom":[subQ1,subQ3]});Q3=makeQuery(id+"F6.imprint","IMPRINT",FACE,{"disambiguationData":[TD([[makeQuery(id+"F6.imprint","IMPRINT",EDGE,{"disambiguationData":[TD([[subQ5,-1.0]])],"derivedFrom":subQ1}),1.0]])]});}
            var Q4;
            {var subQ1=sQuery(id+"F6.wireOp",EDGE,"E31.13");var subQ3=sQuery(id+"F6.wireOp",EDGE,"E40.0.MirrorC");var subQ5=makeQuery(id+"F6.imprint","INTERSECT",VERTEX,{"derivedFrom":[subQ1,subQ3]});Q4=makeQuery(id+"F6.imprint","IMPRINT",FACE,{"disambiguationData":[TD([[makeQuery(id+"F6.imprint","IMPRINT",EDGE,{"disambiguationData":[TD([[subQ5,-1.0]])],"derivedFrom":subQ1}),-1.0]])]});}
            var Q5;
            {var subQ0=sQuery(id+"F6.wireOp",EDGE,"E47.0.MirrorCS");var subQ1=sQuery(id+"F6.wireOp",EDGE,"E31.13");var subQ2=makeQuery(id+"F6.imprint","INTERSECT",VERTEX,{"derivedFrom":[subQ1,subQ0]});Q5=makeQuery(id+"F6.imprint","IMPRINT",FACE,{"disambiguationData":[TD([[makeQuery(id+"F6.imprint","IMPRINT",EDGE,{"disambiguationData":[TD([[subQ2,-1.0]])],"derivedFrom":subQ1}),-1.0]])]});}
            var Q6;
            {var subQ0=sQuery(id+"F6.wireOp",EDGE,"E46.0.MirrorCS");var subQ1=sQuery(id+"F6.wireOp",EDGE,"E31.17");var subQ2=makeQuery(id+"F6.imprint","INTERSECT",VERTEX,{"derivedFrom":[subQ1,subQ0]});Q6=makeQuery(id+"F6.imprint","IMPRINT",FACE,{"disambiguationData":[TD([[makeQuery(id+"F6.imprint","IMPRINT",EDGE,{"disambiguationData":[TD([[subQ2,-1.0]])],"derivedFrom":subQ1}),1.0]])]});}
            var Q7;
            {var subQ0=sQuery(id+"F6.wireOp",EDGE,"E33");var subQ1=sQuery(id+"F6.wireOp",EDGE,"E31.17");var subQ2=makeQuery(id+"F6.imprint","INTERSECT",VERTEX,{"derivedFrom":[subQ1,subQ0]});Q7=makeQuery(id+"F6.imprint","IMPRINT",FACE,{"disambiguationData":[TD([[makeQuery(id+"F6.imprint","IMPRINT",EDGE,{"disambiguationData":[TD([[subQ2,-1.0]])],"derivedFrom":subQ1}),1.0]])]});}
            var Q8;
            {var subQ1=sQuery(id+"F6.wireOp",EDGE,"E31.21");var subQ3=sQuery(id+"F6.wireOp",EDGE,"E33");var subQ5=makeQuery(id+"F6.imprint","INTERSECT",VERTEX,{"derivedFrom":[subQ1,subQ3]});Q8=makeQuery(id+"F6.imprint","IMPRINT",FACE,{"disambiguationData":[TD([[makeQuery(id+"F6.imprint","IMPRINT",EDGE,{"disambiguationData":[TD([[subQ5,-1.0]])],"derivedFrom":subQ1}),-1.0]])]});}
            extrude(context, id + "F12", {"entities" : qUnion([Q0, Q1, Q2, Q3, Q4, Q5, Q6, Q7, Q8]), "operationType" : NewBodyOperationType.ADD, "oppositeDirection" : true, "depth" : 1 * mm});
        }
        {
            var Q0;
            Q0=makeQuery(id+"F12.opExtrude","SWEPT_EDGE",EDGE,{"disambiguationData":[OSD([sQuery(id+"F6.wireOp",EDGE,"E31.15"),sQuery(id+"F6.wireOp",EDGE,"E31.17")])]});
            var Q1;
            Q1=makeQuery(id+"F12.opExtrude","SWEPT_EDGE",EDGE,{"disambiguationData":[OSD([sQuery(id+"F6.wireOp",EDGE,"E31.13"),sQuery(id+"F6.wireOp",EDGE,"E31.15")])]});
            var Q2;
            {var subQ0=sQuery(id+"F6.wireOp",EDGE,"E41.2");var subQ1=sQuery(id+"F6.wireOp",EDGE,"E41.3");Q2=makeQuery(id+"F12.boolean.opBoolean","MERGE",EDGE,{"derivedFrom":[makeQuery(id+"F7.opExtrude","SWEPT_EDGE",EDGE,{"disambiguationData":[OSD([subQ0,subQ1])]}),makeQuery(id+"F12.opExtrude","SWEPT_EDGE",EDGE,{"disambiguationData":[OSD([subQ0,subQ1])]})]});}
            var Q3;
            {var subQ0=sQuery(id+"F6.wireOp",EDGE,"E41.1");var subQ1=sQuery(id+"F6.wireOp",EDGE,"E41.2");Q3=makeQuery(id+"F12.boolean.opBoolean","MERGE",EDGE,{"derivedFrom":[makeQuery(id+"F7.opExtrude","SWEPT_EDGE",EDGE,{"disambiguationData":[OSD([subQ0,subQ1])]}),makeQuery(id+"F12.opExtrude","SWEPT_EDGE",EDGE,{"disambiguationData":[OSD([subQ0,subQ1])]})]});}
            var Q4;
            Q4=makeQuery(id+"F12.opExtrude","SWEPT_EDGE",EDGE,{"disambiguationData":[OSD([sQuery(id+"F6.wireOp",EDGE,"E31.17"),sQuery(id+"F6.wireOp",EDGE,"E31.18")])]});
            var Q5;
            Q5=makeQuery(id+"F12.opExtrude","SWEPT_EDGE",EDGE,{"disambiguationData":[OSD([sQuery(id+"F6.wireOp",EDGE,"E31.18"),sQuery(id+"F6.wireOp",EDGE,"E31.21")])]});
            var Q6;
            {var subQ0=sQuery(id+"F6.wireOp",EDGE,"E41.0");var subQ1=sQuery(id+"F6.wireOp",EDGE,"E41.1");Q6=makeQuery(id+"F12.boolean.opBoolean","MERGE",EDGE,{"derivedFrom":[makeQuery(id+"F7.opExtrude","SWEPT_EDGE",EDGE,{"disambiguationData":[OSD([subQ0,subQ1])]}),makeQuery(id+"F12.opExtrude","SWEPT_EDGE",EDGE,{"disambiguationData":[OSD([subQ0,subQ1])]})]});}
            var Q7;
            {var subQ0=sQuery(id+"F6.wireOp",EDGE,"E41.0");var subQ1=sQuery(id+"F6.wireOp",EDGE,"E41.5");Q7=makeQuery(id+"F12.boolean.opBoolean","MERGE",EDGE,{"derivedFrom":[makeQuery(id+"F7.opExtrude","SWEPT_EDGE",EDGE,{"disambiguationData":[OSD([subQ0,subQ1])]}),makeQuery(id+"F12.opExtrude","SWEPT_EDGE",EDGE,{"disambiguationData":[OSD([subQ0,subQ1])]})]});}
            var Q8;
            {var subQ0=sQuery(id+"F6.wireOp",EDGE,"E41.3");var subQ1=sQuery(id+"F6.wireOp",EDGE,"E41.4");Q8=makeQuery(id+"F12.boolean.opBoolean","MERGE",EDGE,{"derivedFrom":[makeQuery(id+"F7.opExtrude","SWEPT_EDGE",EDGE,{"disambiguationData":[OSD([subQ0,subQ1])]}),makeQuery(id+"F12.opExtrude","SWEPT_EDGE",EDGE,{"disambiguationData":[OSD([subQ0,subQ1])]})]});}
            var Q9;
            {var subQ0=sQuery(id+"F6.wireOp",EDGE,"E41.4");var subQ1=sQuery(id+"F6.wireOp",EDGE,"E41.6");Q9=makeQuery(id+"F12.boolean.opBoolean","MERGE",EDGE,{"derivedFrom":[makeQuery(id+"F7.opExtrude","SWEPT_EDGE",EDGE,{"disambiguationData":[OSD([subQ0,subQ1])]}),makeQuery(id+"F12.opExtrude","SWEPT_EDGE",EDGE,{"disambiguationData":[OSD([subQ0,subQ1])]})]});}
            var Q10;
            Q10=makeQuery(id+"F12.opExtrude","SWEPT_EDGE",EDGE,{"disambiguationData":[OSD([sQuery(id+"F6.wireOp",EDGE,"E31.12"),sQuery(id+"F6.wireOp",EDGE,"E31.13")])]});
            var Q11;
            Q11=makeQuery(id+"F12.opExtrude","SWEPT_EDGE",EDGE,{"disambiguationData":[OSD([sQuery(id+"F6.wireOp",EDGE,"E31.11"),sQuery(id+"F6.wireOp",EDGE,"E31.12")])]});
            var Q12;
            Q12=makeQuery(id+"F12.opExtrude","SWEPT_EDGE",EDGE,{"disambiguationData":[OSD([sQuery(id+"F6.wireOp",EDGE,"E31.10"),sQuery(id+"F6.wireOp",EDGE,"E31.21")])]});
            var Q13;
            Q13=makeQuery(id+"F12.opExtrude","SWEPT_EDGE",EDGE,{"disambiguationData":[OSD([sQuery(id+"F6.wireOp",EDGE,"E31.10"),sQuery(id+"F6.wireOp",EDGE,"E31.11")])]});
            var Q14;
            {var subQ0=sQuery(id+"F6.wireOp",EDGE,"E41.6");var subQ1=sQuery(id+"F6.wireOp",EDGE,"E41.7");Q14=makeQuery(id+"F12.boolean.opBoolean","MERGE",EDGE,{"derivedFrom":[makeQuery(id+"F7.opExtrude","SWEPT_EDGE",EDGE,{"disambiguationData":[OSD([subQ0,subQ1])]}),makeQuery(id+"F12.opExtrude","SWEPT_EDGE",EDGE,{"disambiguationData":[OSD([subQ0,subQ1])]})]});}
            var Q15;
            {var subQ0=sQuery(id+"F6.wireOp",EDGE,"E41.5");var subQ1=sQuery(id+"F6.wireOp",EDGE,"E41.7");Q15=makeQuery(id+"F12.boolean.opBoolean","MERGE",EDGE,{"derivedFrom":[makeQuery(id+"F7.opExtrude","SWEPT_EDGE",EDGE,{"disambiguationData":[OSD([subQ0,subQ1])]}),makeQuery(id+"F12.opExtrude","SWEPT_EDGE",EDGE,{"disambiguationData":[OSD([subQ0,subQ1])]})]});}
            fillet(context, id + "F13", {"entities" : qUnion([Q0, Q1, Q2, Q3, Q4, Q5, Q6, Q7, Q8, Q9, Q10, Q11, Q12, Q13, Q14, Q15]), "radius" : 1 * mm, "tangentPropagation" : true, "allowEdgeOverflow" : false});
        }
    });
